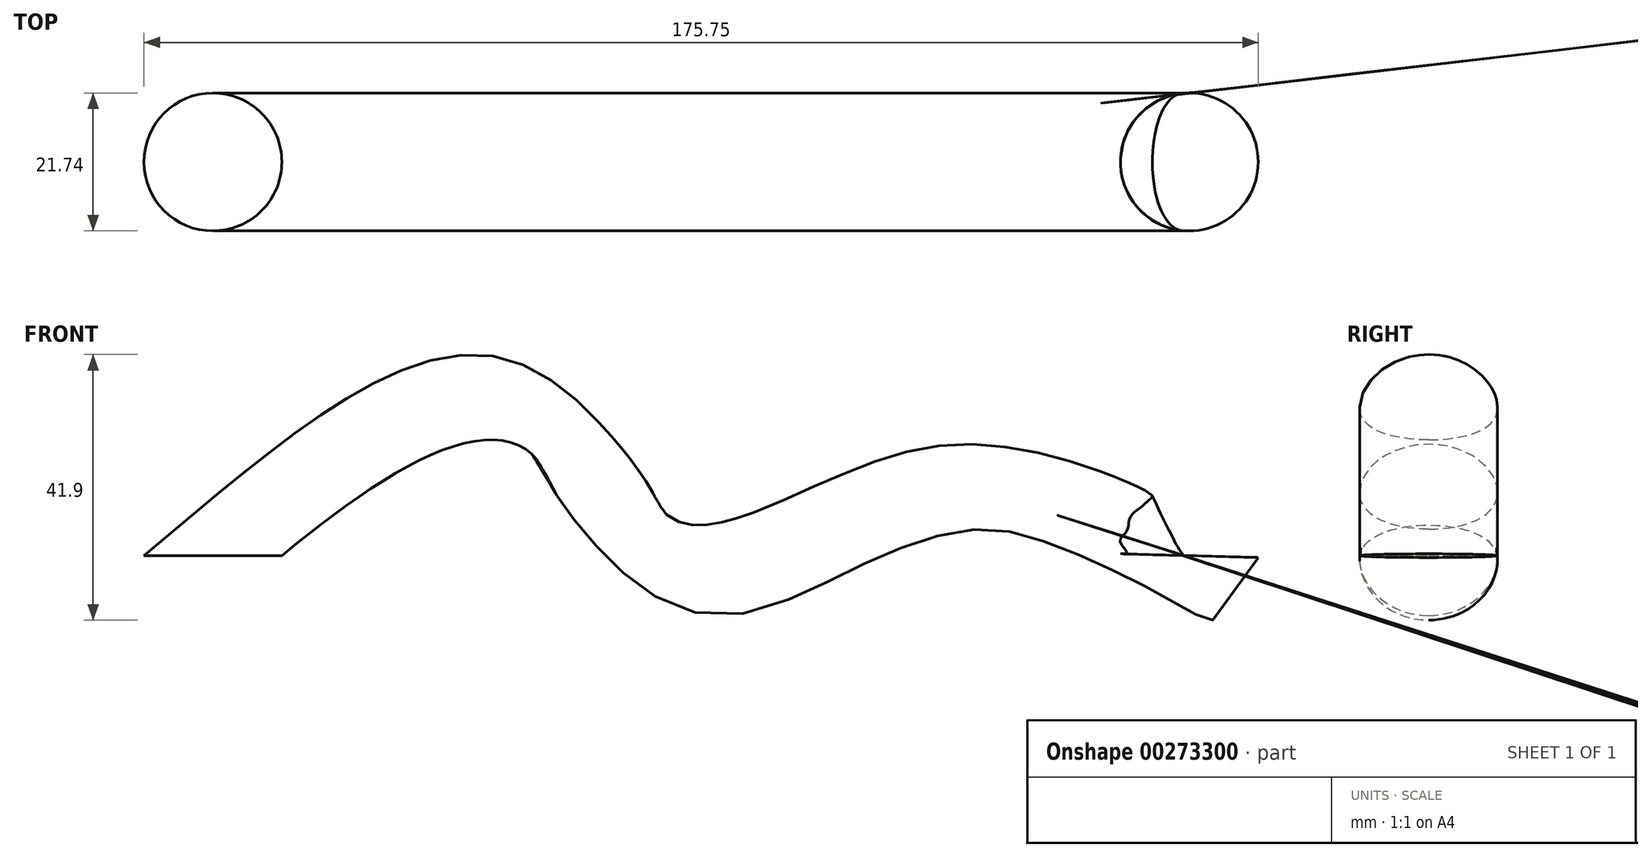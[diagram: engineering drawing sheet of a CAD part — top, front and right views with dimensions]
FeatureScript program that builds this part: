
annotation { "Feature Type Name" : "Feature", "Feature Type Description" : "" }
export const myFeature = defineFeature(function(context is Context, id is Id, definition is map)
    precondition{}
    {
        {
            var Q0;
            Q0=qCreatedBy(makeId("Top.planeOp"),FACE);
            var sketch = newSketch(context, id + "F0", { "sketchPlane" : qUnion([Q0])});
            skCircle(sketch, "E0", {"center": v(-76.24, 0) * mm, "radius": 10.87 * mm});
            skSolve(sketch);
        }
        {
            var Q0;
            Q0=qCreatedBy(makeId("Front.planeOp"),FACE);
            var sketch = newSketch(context, id + "F1", { "sketchPlane" : qUnion([Q0])});
            skFitSpline(sketch, "E1", {"points": [v(-76.81, 0) * mm, v(-29.59, 22.8) * mm, v(0, 0) * mm, v(42.8, 10.34) * mm, v(76.68, 0) * mm, v(77.2, 0) * mm], "startDerivative": vector(199.7, 165.52) * mm, "endDerivative": vector(15.2, 11.92) * mm});
            skSolve(sketch);
        }
        {
            var Q0;
            Q0=makeQuery(id+"F0.imprint","IMPRINT",FACE,{"disambiguationData":[TD([[makeQuery(id+"F0.imprint","IMPRINT",EDGE,{"derivedFrom":sQuery(id+"F0.wireOp",EDGE,"E0")}),1.0]])]});
            var Q1;
            Q1=sQuery(id+"F1.wireOp",EDGE,"E1");
            sweep(context, id + "F2", {"profiles" : qUnion([Q0]), "path" : qUnion([Q1])});
        }
    });
